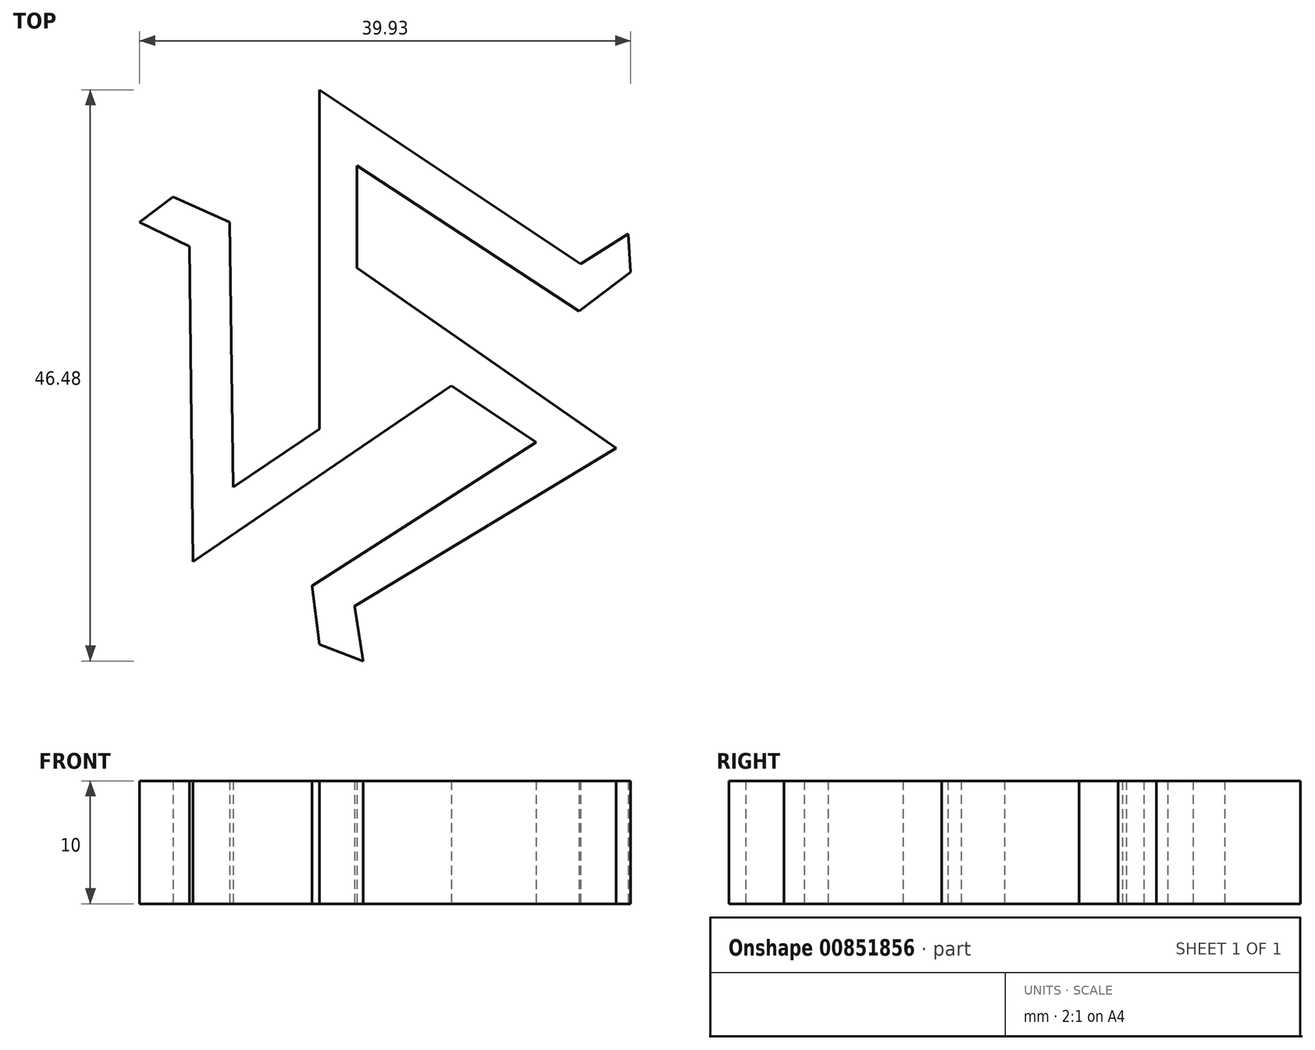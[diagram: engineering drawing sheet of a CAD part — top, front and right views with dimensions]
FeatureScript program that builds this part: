
annotation { "Feature Type Name" : "Feature", "Feature Type Description" : "" }
export const myFeature = defineFeature(function(context is Context, id is Id, definition is map)
    precondition{}
    {
        {
            var Q0;
            Q0=qCreatedBy(makeId("Top.planeOp"),FACE);
            var sketch = newSketch(context, id + "F0", { "sketchPlane" : qUnion([Q0])});
            skLineSegment(sketch, "E0", {"start": v(25, 25) * mm, "end": v(-25, -25) * mm, "construction": true});
            skLineSegment(sketch, "E1", {"start": v(-25, 25) * mm, "end": v(25, -25) * mm, "construction": true});
            skPoint(sketch, "E2", {"position": v(0, 0) * mm});
            skLineSegment(sketch, "E3", {"start": v(20.1, 11.37) * mm, "end": v(16.23, 8.94) * mm});
            skLineSegment(sketch, "E4", {"start": v(16.23, 8.94) * mm, "end": v(-5.01, 23.1) * mm});
            skLineSegment(sketch, "E5", {"start": v(-5.01, 23.1) * mm, "end": v(-5.01, -4.49) * mm});
            skLineSegment(sketch, "E6", {"start": v(-5.01, -4.49) * mm, "end": v(-12.03, -9.23) * mm});
            skLineSegment(sketch, "E7", {"start": v(-12.03, -9.23) * mm, "end": v(-12.32, 12.32) * mm});
            skLineSegment(sketch, "E8", {"start": v(-12.32, 12.32) * mm, "end": v(-16.94, 14.38) * mm});
            skLineSegment(sketch, "E9", {"start": v(-16.94, 14.38) * mm, "end": v(-19.64, 12.32) * mm});
            skLineSegment(sketch, "E10", {"start": v(-19.64, 12.32) * mm, "end": v(-15.59, 10.36) * mm});
            skLineSegment(sketch, "E11", {"start": v(-15.59, 10.36) * mm, "end": v(-15.3, -15.3) * mm});
            skLineSegment(sketch, "E12", {"start": v(-15.3, -15.3) * mm, "end": v(5.71, -0.98) * mm});
            skLineSegment(sketch, "E13", {"start": v(5.71, -0.98) * mm, "end": v(12.6, -5.57) * mm});
            skLineSegment(sketch, "E14", {"start": v(12.6, -5.57) * mm, "end": v(-5.63, -17.27) * mm});
            skLineSegment(sketch, "E15", {"start": v(-5.63, -17.27) * mm, "end": v(-5.01, -22.03) * mm});
            skLineSegment(sketch, "E16", {"start": v(-5.01, -22.03) * mm, "end": v(-1.47, -23.38) * mm});
            skLineSegment(sketch, "E17", {"start": v(-1.47, -23.38) * mm, "end": v(-2.15, -18.9) * mm});
            skLineSegment(sketch, "E18", {"start": v(-2.15, -18.9) * mm, "end": v(19.12, -6.07) * mm});
            skLineSegment(sketch, "E19", {"start": v(19.12, -6.07) * mm, "end": v(-1.97, 8.62) * mm});
            skLineSegment(sketch, "E20", {"start": v(-1.97, 8.62) * mm, "end": v(-1.97, 16.94) * mm});
            skLineSegment(sketch, "E21", {"start": v(-1.97, 16.94) * mm, "end": v(16.1, 5.1) * mm});
            skLineSegment(sketch, "E22", {"start": v(16.1, 5.1) * mm, "end": v(20.3, 8.26) * mm});
            skLineSegment(sketch, "E23", {"start": v(20.3, 8.26) * mm, "end": v(20.1, 11.37) * mm});
            skSolve(sketch);
        }
        {
            var Q0;
            Q0=makeQuery(id+"F0.imprint","IMPRINT",FACE,{"disambiguationData":[TD([[makeQuery(id+"F0.imprint","IMPRINT",EDGE,{"derivedFrom":sQuery(id+"F0.wireOp",EDGE,"E3")}),1.0]])]});
            extrude(context, id + "F1", {"entities" : qUnion([Q0]), "depth" : 10 * mm, "offsetDistance" : 25 * mm});
        }
    });
